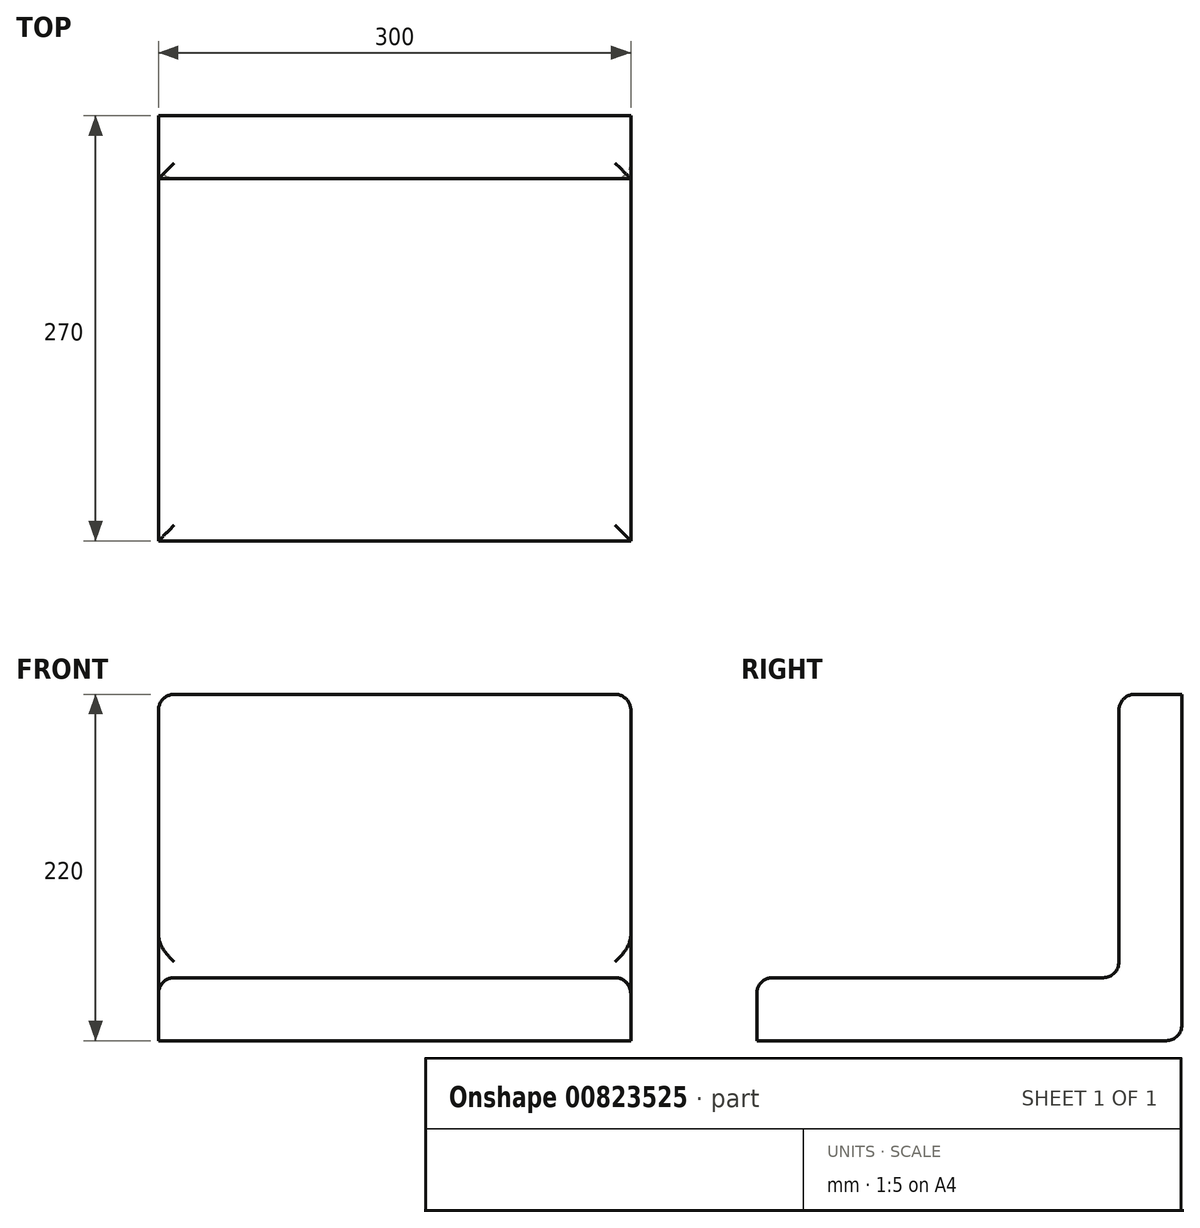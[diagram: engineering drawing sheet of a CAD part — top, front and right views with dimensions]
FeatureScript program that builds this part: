
annotation { "Feature Type Name" : "Feature", "Feature Type Description" : "" }
export const myFeature = defineFeature(function(context is Context, id is Id, definition is map)
    precondition{}
    {
        {
            var Q0;
            Q0=qCreatedBy(makeId("Front.planeOp"),FACE);
            var sketch = newSketch(context, id + "F0", { "sketchPlane" : qUnion([Q0])});
            skLineSegment(sketch, "E0.bottom", {"start": v(154.68, -20) * mm, "end": v(-145.32, -20) * mm});
            skLineSegment(sketch, "E0.top", {"start": v(154.68, 20) * mm, "end": v(-145.32, 20) * mm});
            skLineSegment(sketch, "E0.left", {"start": v(154.68, -20) * mm, "end": v(154.68, 20) * mm});
            skLineSegment(sketch, "E0.right", {"start": v(-145.32, -20) * mm, "end": v(-145.32, 20) * mm});
            skPoint(sketch, "E0.middle", {"position": v(4.68, 0) * mm});
            skSolve(sketch);
        }
        {
            var Q0;
            Q0=qCreatedBy(makeId("Right.planeOp"),FACE);
            var sketch = newSketch(context, id + "F1", { "sketchPlane" : qUnion([Q0])});
            skLineSegment(sketch, "E1", {"start": v(0, 0) * mm, "end": v(250, 0) * mm});
            skLineSegment(sketch, "E2", {"start": v(250, 0) * mm, "end": v(250, 200) * mm});
            skSolve(sketch);
        }
        {
            var Q0;
            Q0=makeQuery(id+"F0.imprint","IMPRINT",FACE,{"disambiguationData":[TD([[makeQuery(id+"F0.imprint","IMPRINT",EDGE,{"derivedFrom":sQuery(id+"F0.wireOp",EDGE,"E0.bottom")}),-1.0]])]});
            var Q1;
            Q1=sQuery(id+"F1.wireOp",EDGE,"E1");
            var Q2;
            Q2=sQuery(id+"F1.wireOp",EDGE,"E2");
            sweep(context, id + "F2", {"profiles" : qUnion([Q0]), "path" : qUnion([Q1, Q2])});
        }
        {
            var Q0;
            Q0=makeQuery(id+"F2.opSweep","CAP_EDGE",EDGE,{"disambiguationData":[OSD([sQuery(id+"F0.wireOp",EDGE,"E0.left"),sQuery(id+"F1.wireOp",VERTEX,"E2.end")])],"isStart":false});
            var Q1;
            Q1=makeQuery(id+"F2.opSweep","CAP_EDGE",EDGE,{"disambiguationData":[OSD([sQuery(id+"F0.wireOp",EDGE,"E0.right"),sQuery(id+"F1.wireOp",VERTEX,"E2.end")])],"isStart":false});
            var Q2;
            Q2=makeQuery(id+"F2.opSweep","SWEPT_EDGE",EDGE,{"disambiguationData":[OSD([sQuery(id+"F0.wireOp",EDGE,"E0.top"),sQuery(id+"F0.wireOp",EDGE,"E0.left"),sQuery(id+"F1.wireOp",EDGE,"E1")])]});
            var Q3;
            Q3=makeQuery(id+"F2.opSweep","CAP_EDGE",EDGE,{"disambiguationData":[OSD([sQuery(id+"F0.wireOp",EDGE,"E0.top"),sQuery(id+"F1.wireOp",VERTEX,"E1.start")])],"isStart":true});
            var Q4;
            Q4=makeQuery(id+"F2.opSweep","SWEPT_EDGE",EDGE,{"disambiguationData":[OSD([sQuery(id+"F0.wireOp",EDGE,"E0.top"),sQuery(id+"F0.wireOp",EDGE,"E0.right"),sQuery(id+"F1.wireOp",EDGE,"E1")])]});
            var Q5;
            Q5=makeQuery(id+"F2.opSweep","MID_CAP_EDGE",EDGE,{"disambiguationData":[OSD([sQuery(id+"F0.wireOp",EDGE,"E0.bottom"),sQuery(id+"F1.wireOp",VERTEX,"E2.start")])],"capPos":1.0});
            var Q6;
            Q6=makeQuery(id+"F2.opSweep","MID_CAP_EDGE",EDGE,{"disambiguationData":[OSD([sQuery(id+"F0.wireOp",EDGE,"E0.top"),sQuery(id+"F1.wireOp",VERTEX,"E2.start")])],"capPos":1.0});
            var Q7;
            Q7=makeQuery(id+"F2.opSweep","CAP_EDGE",EDGE,{"disambiguationData":[OSD([sQuery(id+"F0.wireOp",EDGE,"E0.top"),sQuery(id+"F1.wireOp",VERTEX,"E2.end")])],"isStart":false});
            fillet(context, id + "F3", {"entities" : qUnion([Q0, Q1, Q2, Q3, Q4, Q5, Q6, Q7]), "radius" : 10 * mm, "tangentPropagation" : true, "allowEdgeOverflow" : false});
        }
    });
